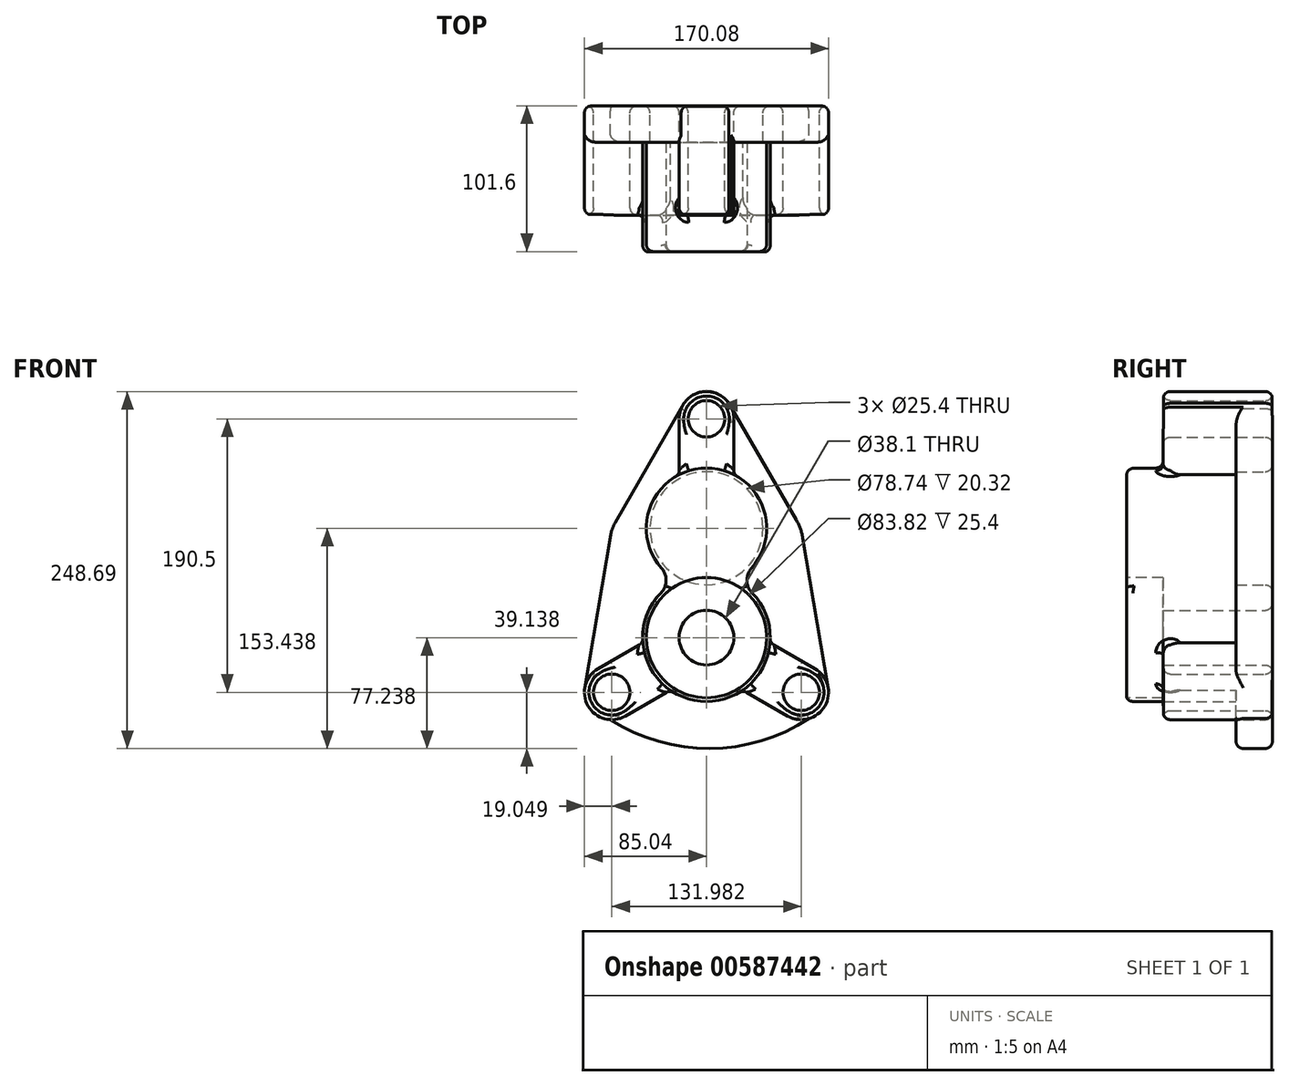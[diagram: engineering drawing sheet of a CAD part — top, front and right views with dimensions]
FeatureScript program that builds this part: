
annotation { "Feature Type Name" : "Feature", "Feature Type Description" : "" }
export const myFeature = defineFeature(function(context is Context, id is Id, definition is map)
    precondition{}
    {
        {
            var Q0;
            Q0=qCreatedBy(makeId("Front.planeOp"),FACE);
            var sketch = newSketch(context, id + "F0", { "sketchPlane" : qUnion([Q0])});
            skArc(sketch, "E0", {"start": v(-20.3, -6.9) * mm, "mid": v(0, -90.88) * mm, "end": v(20.3, -6.9) * mm});
            skArc(sketch, "E1", {"start": v(-17.46, -8.33) * mm, "mid": v(0, -88.34) * mm, "end": v(17.46, -8.33) * mm});
            skCircle(sketch, "E2", {"center": v(0, -46.43) * mm, "radius": 19.05 * mm});
            skCircle(sketch, "E3", {"center": v(0, 29.77) * mm, "radius": 41.91 * mm});
            skCircle(sketch, "E4", {"center": v(0, 29.77) * mm, "radius": 39.37 * mm});
            skLineSegment(sketch, "E5", {"start": v(0, 29.77) * mm, "end": v(0, 105.97) * mm, "construction": true});
            skLineSegment(sketch, "E6", {"start": v(0, -46.43) * mm, "end": v(-66, -84.53) * mm, "construction": true});
            skLineSegment(sketch, "E7", {"start": v(0, -46.43) * mm, "end": v(66, -84.53) * mm, "construction": true});
            skCircle(sketch, "E8", {"center": v(0, 105.97) * mm, "radius": 12.7 * mm});
            skCircle(sketch, "E9", {"center": v(0, 105.97) * mm, "radius": 19.05 * mm});
            skCircle(sketch, "E10", {"center": v(66, -84.53) * mm, "radius": 12.7 * mm});
            skCircle(sketch, "E11", {"center": v(66, -84.53) * mm, "radius": 19.05 * mm});
            skCircle(sketch, "E12", {"center": v(-66, -84.53) * mm, "radius": 19.05 * mm});
            skCircle(sketch, "E13", {"center": v(-66, -84.53) * mm, "radius": 12.7 * mm});
            skLineSegment(sketch, "E14", {"start": v(-19.05, 105.97) * mm, "end": v(-19.05, 67.1) * mm});
            skLineSegment(sketch, "E15", {"start": v(19.05, 105.97) * mm, "end": v(19.05, 67.1) * mm});
            skLineSegment(sketch, "E16", {"start": v(-75.52, -68.03) * mm, "end": v(-44.3, -50.01) * mm});
            skLineSegment(sketch, "E17", {"start": v(-56.47, -101.03) * mm, "end": v(-25.26, -83.01) * mm});
            skLineSegment(sketch, "E18", {"start": v(56.47, -101.03) * mm, "end": v(25.26, -83.01) * mm});
            skLineSegment(sketch, "E19", {"start": v(75.52, -68.03) * mm, "end": v(44.3, -50.01) * mm});
            skArc(sketch, "E20", {"start": v(-66.95, -103.56) * mm, "mid": v(2.34, -123.67) * mm, "end": v(71.4, -102.8) * mm});
            skLineSegment(sketch, "E21", {"start": v(15.65, 116.82) * mm, "end": v(62.5, 35.7) * mm});
            skLineSegment(sketch, "E22", {"start": v(67.08, 23.01) * mm, "end": v(84.77, -81.35) * mm});
            skLineSegment(sketch, "E23", {"start": v(-17.65, 113.13) * mm, "end": v(-63.63, 33.73) * mm});
            skLineSegment(sketch, "E24", {"start": v(-66.7, 25.25) * mm, "end": v(-84.77, -81.35) * mm});
            skLineSegment(sketch, "E25", {"start": v(-65.93, 29.77) * mm, "end": v(65.93, 29.77) * mm, "construction": true});
            skPoint(sketch, "E26.visualSharp", {"position": v(-65.93, 29.77) * mm});
            skArc(sketch, "E26.filletArc", {"start": v(-63.63, 33.73) * mm, "mid": v(-65.55, 29.63) * mm, "end": v(-66.7, 25.25) * mm});
            skPoint(sketch, "E27.visualSharp", {"position": v(65.93, 29.77) * mm});
            skArc(sketch, "E27.filletArc", {"start": v(67.08, 23.01) * mm, "mid": v(65.36, 29.56) * mm, "end": v(62.5, 35.7) * mm});
            skArc(sketch, "E28", {"start": v(-17.46, -8.33) * mm, "mid": v(0, -4.52) * mm, "end": v(17.46, -8.33) * mm, "construction": true});
            skArc(sketch, "E29", {"start": v(-20.3, -6.9) * mm, "mid": v(0, -1.98) * mm, "end": v(20.3, -6.9) * mm, "construction": true});
            skSolve(sketch);
        }
        {
            var Q0;
            Q0=makeQuery(id+"F0.imprint","IMPRINT",FACE,{"disambiguationData":[TD([[makeQuery(id+"F0.imprint","IMPRINT",EDGE,{"derivedFrom":sQuery(id+"F0.wireOp",EDGE,"E4")}),1.0]])]});
            var Q1;
            Q1=makeQuery(id+"F0.imprint","IMPRINT",FACE,{"disambiguationData":[TD([[makeQuery(id+"F0.imprint","IMPRINT",EDGE,{"derivedFrom":sQuery(id+"F0.wireOp",EDGE,"E4")}),-1.0]])]});
            var Q2;
            {var subQ0=sQuery(id+"F0.wireOp",EDGE,"E1");Q2=makeQuery(id+"F0.imprint","IMPRINT",FACE,{"disambiguationData":[TD([[makeQuery(id+"F0.imprint","IMPRINT",EDGE,{"derivedFrom":subQ0}),1.0]])]});}
            var Q3;
            {var subQ8=sQuery(id+"F0.wireOp",EDGE,"E1");Q3=makeQuery(id+"F0.imprint","IMPRINT",FACE,{"disambiguationData":[TD([[makeQuery(id+"F0.imprint","IMPRINT",EDGE,{"derivedFrom":subQ8}),-1.0]])]});}
            extrude(context, id + "F1", {"entities" : qUnion([Q0, Q1, Q2, Q3]), "depth" : 101.6 * mm, "offsetDistance" : 25.4 * mm});
        }
        {
            var Q0;
            {var subQ0=sQuery(id+"F0.wireOp",EDGE,"E3");var subQ1=sQuery(id+"F0.wireOp",EDGE,"E0");Q0=makeQuery(id+"F1.opExtrude","SWEPT_EDGE",EDGE,{"disambiguationData":[OSD([subQ1,subQ0]),TDD([makeQuery(id+"F0.imprint","INTERSECT",VERTEX,{"disambiguationData":[OD(1.0)],"derivedFrom":[subQ1,subQ0]})])]});}
            var Q1;
            {var subQ0=sQuery(id+"F0.wireOp",EDGE,"E3");var subQ1=sQuery(id+"F0.wireOp",EDGE,"E0");Q1=makeQuery(id+"F1.opExtrude","SWEPT_EDGE",EDGE,{"disambiguationData":[OSD([subQ1,subQ0]),TDD([makeQuery(id+"F0.imprint","INTERSECT",VERTEX,{"disambiguationData":[OD(0.0)],"derivedFrom":[subQ1,subQ0]})])]});}
            fillet(context, id + "F2", {"entities" : qUnion([Q0, Q1]), "radius" : 12.7 * mm, "tangentPropagation" : true, "allowEdgeOverflow" : false});
        }
        {
            var Q0;
            Q0=makeQuery(id+"F0.imprint","IMPRINT",FACE,{"disambiguationData":[TD([[makeQuery(id+"F0.imprint","IMPRINT",EDGE,{"derivedFrom":sQuery(id+"F0.wireOp",EDGE,"E4")}),1.0]])]});
            extrude(context, id + "F3", {"entities" : qUnion([Q0]), "operationType" : NewBodyOperationType.REMOVE, "depth" : 25.4 * mm, "offsetDistance" : 25.4 * mm});
        }
        {
            var Q0;
            Q0=makeQuery(id+"F1.opExtrude","CAP_FACE",FACE,{"disambiguationData":[OSD([sQuery(id+"F0.wireOp",EDGE,"E0"),sQuery(id+"F0.wireOp",EDGE,"E2"),sQuery(id+"F0.wireOp",EDGE,"E3")])],"isStart":false});
            var sketch = newSketch(context, id + "F4", { "sketchPlane" : qUnion([Q0])});
            skArc(sketch, "E30.0.1", {"start": v(-17.46, -8.33) * mm, "mid": v(0, -88.34) * mm, "end": v(17.46, -8.33) * mm});
            skArc(sketch, "E31", {"start": v(-17.46, -8.33) * mm, "mid": v(0, -4.52) * mm, "end": v(17.46, -8.33) * mm});
            skSolve(sketch);
        }
        {
            var Q0;
            Q0=makeQuery(id+"F4.imprint","IMPRINT",FACE,{"disambiguationData":[TD([[makeQuery(id+"F4.imprint","IMPRINT",EDGE,{"derivedFrom":sQuery(id+"F4.wireOp",EDGE,"E30.0.1")}),1.0]])]});
            extrude(context, id + "F5", {"entities" : qUnion([Q0]), "operationType" : NewBodyOperationType.REMOVE, "oppositeDirection" : true, "depth" : 25.4 * mm, "offsetDistance" : 25.4 * mm});
        }
        {
            var Q0;
            {var subQ0=sQuery(id+"F0.wireOp",EDGE,"E14");Q0=makeQuery(id+"F0.imprint","IMPRINT",FACE,{"disambiguationData":[TD([[makeQuery(id+"F0.imprint","IMPRINT",EDGE,{"derivedFrom":subQ0}),1.0]])]});}
            var Q1;
            Q1=makeQuery(id+"F0.imprint","IMPRINT",FACE,{"disambiguationData":[TD([[makeQuery(id+"F0.imprint","IMPRINT",EDGE,{"derivedFrom":sQuery(id+"F0.wireOp",EDGE,"E8")}),-1.0]])]});
            var Q2;
            Q2=makeQuery(id+"F0.imprint","IMPRINT",FACE,{"disambiguationData":[TD([[makeQuery(id+"F0.imprint","IMPRINT",EDGE,{"derivedFrom":sQuery(id+"F0.wireOp",EDGE,"E13")}),-1.0]])]});
            var Q3;
            {var subQ0=sQuery(id+"F0.wireOp",EDGE,"E16");Q3=makeQuery(id+"F0.imprint","IMPRINT",FACE,{"disambiguationData":[TD([[makeQuery(id+"F0.imprint","IMPRINT",EDGE,{"derivedFrom":subQ0}),-1.0]])]});}
            var Q4;
            {var subQ0=sQuery(id+"F0.wireOp",EDGE,"E18");Q4=makeQuery(id+"F0.imprint","IMPRINT",FACE,{"disambiguationData":[TD([[makeQuery(id+"F0.imprint","IMPRINT",EDGE,{"derivedFrom":subQ0}),-1.0]])]});}
            var Q5;
            Q5=makeQuery(id+"F0.imprint","IMPRINT",FACE,{"disambiguationData":[TD([[makeQuery(id+"F0.imprint","IMPRINT",EDGE,{"derivedFrom":sQuery(id+"F0.wireOp",EDGE,"E10")}),-1.0]])]});
            extrude(context, id + "F6", {"entities" : qUnion([Q0, Q1, Q2, Q3, Q4, Q5]), "operationType" : NewBodyOperationType.ADD, "depth" : 76.2 * mm, "offsetDistance" : 25.4 * mm});
        }
        {
            var Q0;
            {var subQ0=sQuery(id+"F0.wireOp",EDGE,"E14");Q0=makeQuery(id+"F0.imprint","IMPRINT",FACE,{"disambiguationData":[TD([[makeQuery(id+"F0.imprint","IMPRINT",EDGE,{"derivedFrom":subQ0}),-1.0]])]});}
            var Q1;
            {var subQ4=sQuery(id+"F0.wireOp",EDGE,"E15");Q1=makeQuery(id+"F0.imprint","IMPRINT",FACE,{"disambiguationData":[TD([[makeQuery(id+"F0.imprint","IMPRINT",EDGE,{"derivedFrom":subQ4}),1.0]])]});}
            var Q2;
            {var subQ0=sQuery(id+"F0.wireOp",EDGE,"E17");Q2=makeQuery(id+"F0.imprint","IMPRINT",FACE,{"disambiguationData":[TD([[makeQuery(id+"F0.imprint","IMPRINT",EDGE,{"derivedFrom":subQ0}),-1.0]])]});}
            extrude(context, id + "F7", {"entities" : qUnion([Q0, Q1, Q2]), "operationType" : NewBodyOperationType.ADD, "depth" : 25.4 * mm, "offsetDistance" : 25.4 * mm});
        }
        {
            var Q0;
            Q0=makeQuery(id+"F1.opExtrude","CAP_EDGE",EDGE,{"disambiguationData":[OSD([sQuery(id+"F0.wireOp",EDGE,"E3")])],"isStart":false});
            var Q1;
            Q1=makeQuery(id+"F6.opExtrude","CAP_FACE",FACE,{"disambiguationData":[OSD([sQuery(id+"F0.wireOp",EDGE,"E3"),sQuery(id+"F0.wireOp",EDGE,"E8"),sQuery(id+"F0.wireOp",EDGE,"E9"),sQuery(id+"F0.wireOp",EDGE,"E14"),sQuery(id+"F0.wireOp",EDGE,"E15"),sQuery(id+"F0.wireOp",EDGE,"E21")])],"isStart":false});
            var Q2;
            Q2=makeQuery(id+"F6.opExtrude","CAP_FACE",FACE,{"disambiguationData":[OSD([sQuery(id+"F0.wireOp",EDGE,"E0"),sQuery(id+"F0.wireOp",EDGE,"E10"),sQuery(id+"F0.wireOp",EDGE,"E11"),sQuery(id+"F0.wireOp",EDGE,"E18"),sQuery(id+"F0.wireOp",EDGE,"E19")])],"isStart":false});
            var Q3;
            Q3=makeQuery(id+"F6.opExtrude","CAP_FACE",FACE,{"disambiguationData":[OSD([sQuery(id+"F0.wireOp",EDGE,"E0"),sQuery(id+"F0.wireOp",EDGE,"E12"),sQuery(id+"F0.wireOp",EDGE,"E13"),sQuery(id+"F0.wireOp",EDGE,"E16"),sQuery(id+"F0.wireOp",EDGE,"E17")])],"isStart":false});
            var Q4;
            {var subQ0=sQuery(id+"F0.wireOp",EDGE,"E21");var subQ1=sQuery(id+"F0.wireOp",EDGE,"E19");var subQ2=sQuery(id+"F0.wireOp",EDGE,"E15");var subQ3=sQuery(id+"F0.wireOp",EDGE,"E11");var subQ4=sQuery(id+"F0.wireOp",EDGE,"E9");var subQ5=sQuery(id+"F0.wireOp",EDGE,"E3");var subQ6=sQuery(id+"F0.wireOp",EDGE,"E0");var subQ7=sQuery(id+"F0.wireOp",EDGE,"E18");var subQ8=sQuery(id+"F0.wireOp",EDGE,"E17");var subQ9=sQuery(id+"F0.wireOp",EDGE,"E12");var subQ10=sQuery(id+"F0.wireOp",EDGE,"E16");var subQ11=sQuery(id+"F0.wireOp",EDGE,"E14");Q4=makeQuery(id+"F7.boolean.opBoolean","MERGE",FACE,{"derivedFrom":[makeQuery(id+"F6.boolean.opBoolean","MERGE",FACE,{"derivedFrom":[makeQuery(id+"F1.opExtrude","CAP_FACE",FACE,{"disambiguationData":[OSD([subQ6,sQuery(id+"F0.wireOp",EDGE,"E2"),subQ5])],"isStart":true}),makeQuery(id+"F6.opExtrude","CAP_FACE",FACE,{"disambiguationData":[OSD([subQ6,subQ9,sQuery(id+"F0.wireOp",EDGE,"E13"),subQ10,subQ8])],"isStart":true}),makeQuery(id+"F6.opExtrude","CAP_FACE",FACE,{"disambiguationData":[OSD([subQ6,sQuery(id+"F0.wireOp",EDGE,"E10"),subQ3,subQ7,subQ1])],"isStart":true}),makeQuery(id+"F6.opExtrude","CAP_FACE",FACE,{"disambiguationData":[OSD([subQ5,sQuery(id+"F0.wireOp",EDGE,"E8"),subQ4,subQ11,subQ2,subQ0])],"isStart":true})]}),makeQuery(id+"F7.opExtrude","CAP_FACE",FACE,{"disambiguationData":[OSD([subQ6,subQ5,subQ4,subQ9,subQ11,subQ10,sQuery(id+"F0.wireOp",EDGE,"E23"),sQuery(id+"F0.wireOp",EDGE,"E24"),sQuery(id+"F0.wireOp",EDGE,"E26.filletArc")])],"isStart":true}),makeQuery(id+"F7.opExtrude","CAP_FACE",FACE,{"disambiguationData":[OSD([subQ6,subQ3,subQ9,subQ8,subQ7,sQuery(id+"F0.wireOp",EDGE,"E20")])],"isStart":true}),makeQuery(id+"F7.opExtrude","CAP_FACE",FACE,{"disambiguationData":[OSD([subQ6,subQ5,subQ4,subQ3,subQ2,subQ1,subQ0,sQuery(id+"F0.wireOp",EDGE,"E22"),sQuery(id+"F0.wireOp",EDGE,"E27.filletArc")])],"isStart":true})]});}
            var Q5;
            {var subQ0=sQuery(id+"F0.wireOp",EDGE,"E3");Q5=makeQuery(id+"F7.opExtrude","CAP_EDGE",EDGE,{"disambiguationData":[OSD([subQ0]),TDD([makeQuery(id+"F0.imprint","IMPRINT",EDGE,{"disambiguationData":[TD([[makeQuery(id+"F0.imprint","INTERSECT",VERTEX,{"disambiguationData":[OD(1.0)],"derivedFrom":[sQuery(id+"F0.wireOp",EDGE,"E0"),subQ0]}),-1.0]])],"derivedFrom":subQ0})])],"isStart":false});}
            var Q6;
            Q6=makeQuery(id+"F7.opExtrude","CAP_EDGE",EDGE,{"disambiguationData":[OSD([sQuery(id+"F0.wireOp",EDGE,"E15")])],"isStart":false});
            var Q7;
            {var subQ0=sQuery(id+"F0.wireOp",EDGE,"E0");Q7=makeQuery(id+"F7.opExtrude","CAP_EDGE",EDGE,{"disambiguationData":[OSD([subQ0]),TDD([makeQuery(id+"F0.imprint","IMPRINT",EDGE,{"disambiguationData":[TD([[makeQuery(id+"F0.imprint","INTERSECT",VERTEX,{"derivedFrom":[subQ0,sQuery(id+"F0.wireOp",EDGE,"E17")]}),-1.0]])],"derivedFrom":subQ0})])],"isStart":false});}
            var Q8;
            Q8=makeQuery(id+"F7.opExtrude","CAP_EDGE",EDGE,{"disambiguationData":[OSD([sQuery(id+"F0.wireOp",EDGE,"E17")])],"isStart":false});
            var Q9;
            Q9=makeQuery(id+"F7.opExtrude","CAP_EDGE",EDGE,{"disambiguationData":[OSD([sQuery(id+"F0.wireOp",EDGE,"E18")])],"isStart":false});
            var Q10;
            Q10=makeQuery(id+"F7.opExtrude","CAP_EDGE",EDGE,{"disambiguationData":[OSD([sQuery(id+"F0.wireOp",EDGE,"E16")])],"isStart":false});
            var Q11;
            {var subQ0=sQuery(id+"F0.wireOp",EDGE,"E0");Q11=makeQuery(id+"F7.opExtrude","CAP_EDGE",EDGE,{"disambiguationData":[OSD([subQ0]),TDD([makeQuery(id+"F0.imprint","IMPRINT",EDGE,{"disambiguationData":[TD([[makeQuery(id+"F0.imprint","INTERSECT",VERTEX,{"disambiguationData":[OD(0.0)],"derivedFrom":[subQ0,sQuery(id+"F0.wireOp",EDGE,"E3")]}),-1.0]])],"derivedFrom":subQ0})])],"isStart":false});}
            var Q12;
            Q12=makeQuery(id+"F7.opExtrude","CAP_EDGE",EDGE,{"disambiguationData":[OSD([sQuery(id+"F0.wireOp",EDGE,"E14")])],"isStart":false});
            fillet(context, id + "F8", {"entities" : qUnion([Q0, Q1, Q2, Q3, Q4, Q5, Q6, Q7, Q8, Q9, Q10, Q11, Q12]), "radius" : 5.08 * mm, "tangentPropagation" : true, "allowEdgeOverflow" : false});
        }
        {
            var Q0;
            Q0=makeQuery(id+"F7.opExtrude","CAP_EDGE",EDGE,{"disambiguationData":[OSD([sQuery(id+"F0.wireOp",EDGE,"E20")])],"isStart":false});
            var Q1;
            Q1=makeQuery(id+"F7.opExtrude","CAP_EDGE",EDGE,{"disambiguationData":[OSD([sQuery(id+"F0.wireOp",EDGE,"E22")])],"isStart":false});
            var Q2;
            Q2=makeQuery(id+"F7.opExtrude","CAP_EDGE",EDGE,{"disambiguationData":[OSD([sQuery(id+"F0.wireOp",EDGE,"E24")])],"isStart":false});
            fillet(context, id + "F9", {"entities" : qUnion([Q0, Q1, Q2]), "radius" : 5.08 * mm, "tangentPropagation" : true, "allowEdgeOverflow" : false});
        }
    });
